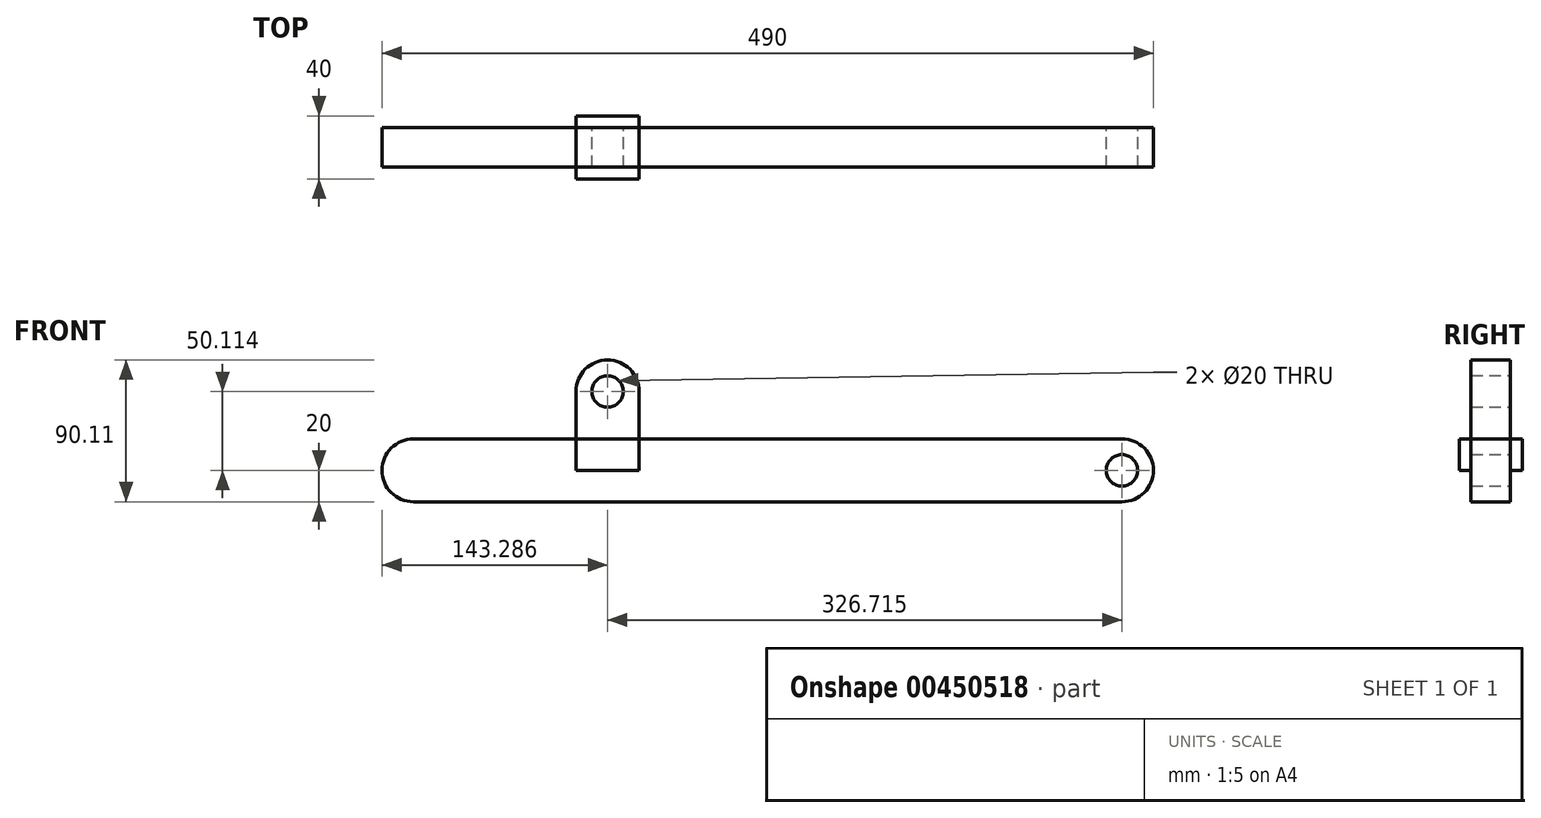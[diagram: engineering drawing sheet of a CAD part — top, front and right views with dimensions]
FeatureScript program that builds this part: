
annotation { "Feature Type Name" : "Feature", "Feature Type Description" : "" }
export const myFeature = defineFeature(function(context is Context, id is Id, definition is map)
    precondition{}
    {
        {
            var Q0;
            Q0=qCreatedBy(makeId("Front.planeOp"),FACE);
            var sketch = newSketch(context, id + "F0", { "sketchPlane" : qUnion([Q0])});
            skLineSegment(sketch, "E0", {"start": v(0, 0) * mm, "end": v(-238.94, 0) * mm});
            skLineSegment(sketch, "E1", {"start": v(-238.94, 0) * mm, "end": v(211.06, 0) * mm});
            skArc(sketch, "E2.0.startCap", {"start": v(-238.94, -20) * mm, "mid": v(-258.94, 0) * mm, "end": v(-238.94, 20) * mm});
            skArc(sketch, "E2.0.endCap", {"start": v(211.06, 20) * mm, "mid": v(231.06, 0) * mm, "end": v(211.06, -20) * mm});
            skLineSegment(sketch, "E2.0.left", {"start": v(-238.94, 20) * mm, "end": v(211.06, 20) * mm});
            skLineSegment(sketch, "E2.0.right", {"start": v(-238.94, -20) * mm, "end": v(211.06, -20) * mm});
            skLineSegment(sketch, "E3", {"start": v(-115.65, 0) * mm, "end": v(-115.65, 50.11) * mm});
            skArc(sketch, "E4.0.startCap", {"start": v(-95.65, 0) * mm, "mid": v(-115.65, -20) * mm, "end": v(-135.65, 0) * mm});
            skArc(sketch, "E4.0.endCap", {"start": v(-135.65, 50.11) * mm, "mid": v(-115.65, 70.11) * mm, "end": v(-95.65, 50.11) * mm});
            skLineSegment(sketch, "E4.0.left", {"start": v(-135.65, 0) * mm, "end": v(-135.65, 50.11) * mm});
            skLineSegment(sketch, "E4.0.right", {"start": v(-95.65, 0) * mm, "end": v(-95.65, 50.11) * mm});
            skSolve(sketch);
        }
        {
            var Q0;
            {var subQ5=sQuery(id+"F0.wireOp",EDGE,"E2.0.endCap");Q0=makeQuery(id+"F0.imprint","IMPRINT",FACE,{"disambiguationData":[TD([[makeQuery(id+"F0.imprint","IMPRINT",EDGE,{"derivedFrom":subQ5}),-1.0]])]});}
            var Q1;
            {var subQ0=sQuery(id+"F0.wireOp",EDGE,"E3");var subQ5=sQuery(id+"F0.wireOp",EDGE,"E2.0.left");var subQ6=makeQuery(id+"F0.imprint","INTERSECT",VERTEX,{"derivedFrom":[subQ5,subQ0]});Q1=makeQuery(id+"F0.imprint","IMPRINT",FACE,{"disambiguationData":[TD([[makeQuery(id+"F0.imprint","IMPRINT",EDGE,{"disambiguationData":[TD([[subQ6,-1.0]])],"derivedFrom":subQ5}),-1.0]])]});}
            var Q2;
            {var subQ3=sQuery(id+"F0.wireOp",EDGE,"E4.0.left");var subQ5=sQuery(id+"F0.wireOp",EDGE,"E2.0.left");var subQ6=makeQuery(id+"F0.imprint","INTERSECT",VERTEX,{"derivedFrom":[subQ5,subQ3]});Q2=makeQuery(id+"F0.imprint","IMPRINT",FACE,{"disambiguationData":[TD([[makeQuery(id+"F0.imprint","IMPRINT",EDGE,{"disambiguationData":[TD([[subQ6,-1.0]])],"derivedFrom":subQ5}),-1.0]])]});}
            var Q3;
            {var subQ0=sQuery(id+"F0.wireOp",EDGE,"E1");var subQ1=makeQuery(id+"F0.imprint","INTERSECT",VERTEX,{"derivedFrom":[subQ0,sQuery(id+"F0.wireOp",EDGE,"E3")]});Q3=makeQuery(id+"F0.imprint","IMPRINT",FACE,{"disambiguationData":[TD([[makeQuery(id+"F0.imprint","IMPRINT",EDGE,{"disambiguationData":[TD([[subQ1,1.0]])],"derivedFrom":subQ0}),-1.0]])]});}
            var Q4;
            {var subQ1=sQuery(id+"F0.wireOp",EDGE,"E2.0.startCap");Q4=makeQuery(id+"F0.imprint","IMPRINT",FACE,{"disambiguationData":[TD([[makeQuery(id+"F0.imprint","IMPRINT",EDGE,{"derivedFrom":subQ1}),-1.0]])]});}
            extrude(context, id + "F1", {"entities" : qUnion([Q0, Q1, Q2, Q3, Q4]), "endBound" : BoundingType.SYMMETRIC, "depth" : 40 * mm});
        }
        {
            var Q0;
            Q0 = qSketchRegion(id + "F0", true);
            extrude(context, id + "F2", {"entities" : qUnion([Q0]), "operationType" : NewBodyOperationType.ADD, "endBound" : BoundingType.SYMMETRIC, "oppositeDirection" : true, "depth" : 25 * mm});
        }
        {
            var Q0;
            Q0=sQuery(id+"F0.wireOp",VERTEX,"E2.0.endCap.center");
            var Q1;
            Q1=sQuery(id+"F0.wireOp",VERTEX,"E4.0.endCap.center");
            var Q2;
            Q2=makeQuery(id+"F1.opExtrude","SWEPT_BODY",BODY,{"disambiguationData":[OSD([sQuery(id+"F0.wireOp",EDGE,"E2.0.startCap"),sQuery(id+"F0.wireOp",EDGE,"E2.0.endCap"),sQuery(id+"F0.wireOp",EDGE,"E2.0.left"),sQuery(id+"F0.wireOp",EDGE,"E2.0.right")])]});
            hole(context, id + "F3", {"style" : HoleStyle.SIMPLE, "endStyle" : HoleEndStyle.THROUGH, "oppositeDirection" : true, "holeDiameter" : 20 * mm, "isTappedThrough" : true, "tappedDepth" : 12 * mm, "tapClearance" : 3, "locations" : qUnion([Q0, Q1]), "scope" : qUnion([Q2])});
        }
        {
            var Q0;
            Q0=sQuery(id+"F0.wireOp",VERTEX,"E4.0.endCap.center");
            var Q1;
            Q1=sQuery(id+"F0.wireOp",VERTEX,"E2.0.endCap.center");
            var Q2;
            Q2=makeQuery(id+"F1.opExtrude","SWEPT_BODY",BODY,{"disambiguationData":[OSD([sQuery(id+"F0.wireOp",EDGE,"E2.0.startCap"),sQuery(id+"F0.wireOp",EDGE,"E2.0.endCap"),sQuery(id+"F0.wireOp",EDGE,"E2.0.left"),sQuery(id+"F0.wireOp",EDGE,"E2.0.right")])]});
            hole(context, id + "F4", {"style" : HoleStyle.SIMPLE, "endStyle" : HoleEndStyle.THROUGH, "holeDiameter" : 20 * mm, "isTappedThrough" : true, "tappedDepth" : 12 * mm, "tapClearance" : 3, "locations" : qUnion([Q0, Q1]), "scope" : qUnion([Q2])});
        }
    });
